# Revit family: Стол медицинский на металлических опорах
name_source: partatom
category: Оборудование
revit_build: Autodesk Revit 2017 (Build: 20170118_1100(x64)
units: mm (PartAtom-declared; Revit-internal decimal feet)

## family parameters
Всегда вертикально = Да
На основе рабочей плоскости = Нет
Общий = Нет
При загрузке вырезать с полостями = Нет
Размер круглого соединителя = Использовать диаметр
Тип детали = Нормальный
Точка расчета площади = Нет

## types (6) — shared parameters
Общ_Высота = 750 мм
Общ_Единицы измерения = шт.
Общ_Наименование = Стол медицинский на металлических регулируемых опорах
Общ_Поставщик = Доктор Мебель

## per-type parameters (varying)
| type | Общ_Глубина | Общ_Тип, марка | Общ_Ширина |
| 600х800 | 600 мм | ДМ-2-006-35 | 800 мм |
| 600х1000 | 600 мм | ДМ-2-006-36 | 1000 мм |
| 600х1200 | 600 мм | ДМ-2-006-37 | 1200 мм |
| 800х1000 | 800 мм | ДМ-2-006-39 | 1000 мм |
| 800х1200 | 800 мм | ДМ-2-006-40 | 1200 мм |
| 800х1600 | 800 мм | ДМ-2-006-41 | 1600 мм |
